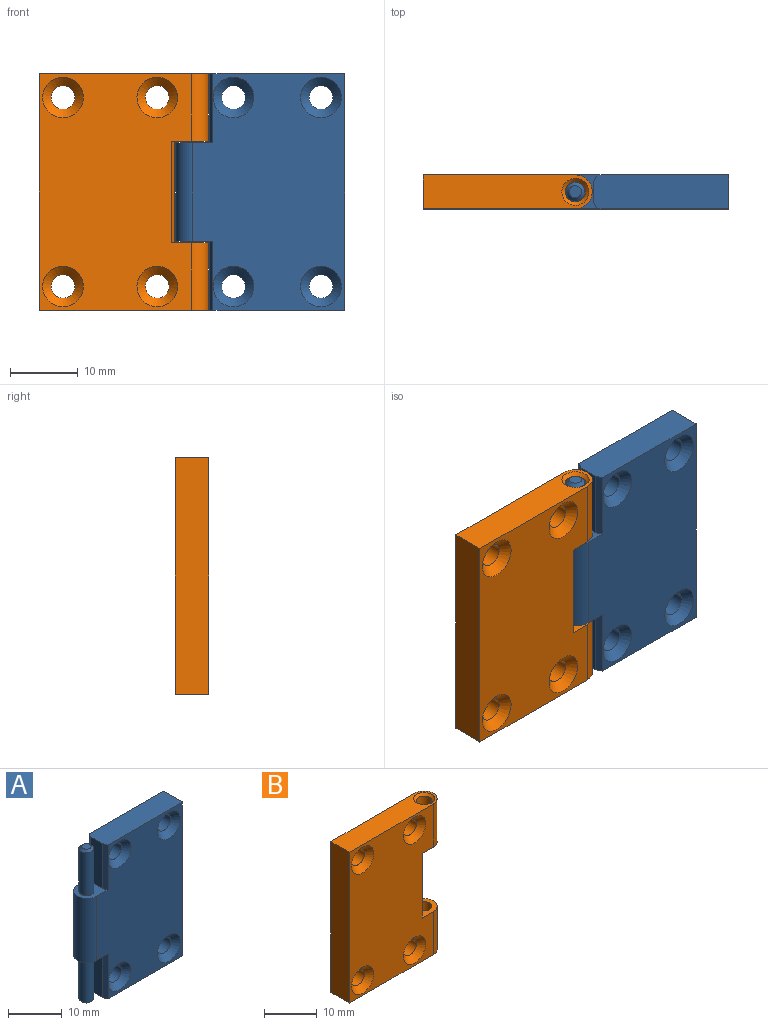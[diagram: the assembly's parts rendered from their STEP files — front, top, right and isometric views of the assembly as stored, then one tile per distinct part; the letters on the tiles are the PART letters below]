
ASSEMBLY  parts=2 mates=1
PART A: 28 faces, bbox 25x5x35 mm
  f0: plane 35x22.5mm, normal (0,-1,0), area 613.2mm2, adj f2,f3,f4,f5,f8,f12,f17,f19
  f1: plane 35x22.5mm, normal (0,1,0), area 687.8mm2, adj f2,f3,f4,f5,f8,f12,f16,f18
  f2: cylinder r=2.5mm len=14.6mm, axis (0,0,1), area 114.7mm2, adj f0,f1,f8,f12
  f3: plane 20x5mm, normal (0,0,-1), area 99.5mm2, adj f0,f1,f4,f10,f24,f26
  f4: plane 35x5mm, normal (1,0,0), area 175mm2, adj f0,f1,f3,f5
  f5: plane 20x5mm, normal (0,0,1), area 99.5mm2, adj f0,f1,f4,f6,f25,f27
  f6: plane 10.2x3mm, normal (-1,0,0), area 30.6mm2, adj f5,f8,f25,f27
  f7: cylinder r=1.4mm len=9.7mm, axis (0,0,1), area 85.3mm2, adj f8,f14
  f8: plane 5.5x5mm, normal (0,0,1), area 16.7mm2, adj f0,f1,f2,f6,f7,f25,f27
  f9: plane 1.8x1.8mm, normal (0,0,1), area 2.5mm2, adj f14
  f10: plane 10.2x3mm, normal (-1,0,0), area 30.6mm2, adj f3,f12,f24,f26
  f11: cylinder r=1.4mm len=9.7mm, axis (0,0,-1), area 85.3mm2, adj f12,f15
  f12: plane 5.5x5mm, normal (0,0,-1), area 16.7mm2, adj f0,f1,f2,f10,f11,f24,f26
  f13: plane 1.8x1.8mm, normal (0,0,-1), area 2.5mm2, adj f15
  f14: cone r=0.9mm half-angle=45deg, axis (0,0,-1), area 5.1mm2, adj f7,f9
  f15: cone r=0.9mm half-angle=45deg, axis (0,0,1), area 5.1mm2, adj f11,f13
  f16: cylinder r=1.75mm len=3.75mm, axis (0,-1,0), area 41.2mm2, adj f1,f17
  f17: cone r=1.75mm half-angle=45deg, axis (0,-1,0), area 26.4mm2, adj f0,f16
  f18: cylinder r=1.75mm len=3.75mm, axis (0,-1,0), area 41.2mm2, adj f1,f19
  f19: cone r=1.75mm half-angle=45deg, axis (0,-1,0), area 26.4mm2, adj f0,f18
  f20: cylinder r=1.75mm len=3.75mm, axis (0,-1,0), area 41.2mm2, adj f1,f21
  f21: cone r=1.75mm half-angle=45deg, axis (0,-1,0), area 26.4mm2, adj f0,f20
  f22: cylinder r=1.75mm len=3.75mm, axis (0,-1,0), area 41.2mm2, adj f1,f23
  f23: cone r=1.75mm half-angle=45deg, axis (0,-1,0), area 26.4mm2, adj f0,f22
  f24: plane 10.2x1mm, normal (-0.89,0.45,0), area 11.4mm2, adj f1,f3,f10,f12
  f25: plane 10.2x1mm, normal (-0.89,0.45,0), area 11.4mm2, adj f1,f5,f6,f8
  f26: plane 10.2x1mm, normal (-0.89,-0.45,0), area 11.4mm2, adj f0,f3,f10,f12
  f27: plane 10.2x1mm, normal (-0.89,-0.45,0), area 11.4mm2, adj f0,f5,f6,f8
PART B: 24 faces, bbox 25x5x35 mm
  f0: plane 15x3mm, normal (1,0,0), area 45mm2, adj f7,f9,f14,f15
  f1: plane 35x5mm, normal (-1,0,0), area 175mm2, adj f2,f3,f4,f5
  f2: plane 25x5mm, normal (0,0,-1), area 109.8mm2, adj f1,f4,f5,f8,f13
  f3: plane 25x5mm, normal (0,0,1), area 109.8mm2, adj f1,f4,f5,f6,f12
  f4: plane 35x22.5mm, normal (0,-1,0), area 629.4mm2, adj f1,f2,f3,f6,f7,f8,f9,f15
  f5: plane 35x22.5mm, normal (0,1,0), area 704mm2, adj f1,f2,f3,f6,f7,f8,f9,f14
  f6: cylinder r=2.5mm len=10mm, axis (0,0,1), area 78.5mm2, adj f3,f4,f5,f7
  f7: plane 5.5x5mm, normal (0,0,-1), area 15.7mm2, adj f0,f4,f5,f6,f11,f14,f15
  f8: cylinder r=2.5mm len=10mm, axis (0,0,-1), area 78.5mm2, adj f2,f4,f5,f9
  f9: plane 5.5x5mm, normal (0,0,1), area 15.7mm2, adj f0,f4,f5,f8,f10,f14,f15
  f10: cylinder r=1.5mm len=9.5mm, axis (0,0,-1), area 89.5mm2, adj f9,f13
  f11: cylinder r=1.5mm len=9.5mm, axis (0,0,-1), area 89.5mm2, adj f7,f12
  f12: cone r=2mm half-angle=45deg, axis (0,0,1), area 7.8mm2, adj f3,f11
  f13: cone r=1.5mm half-angle=45deg, axis (0,0,-1), area 7.8mm2, adj f2,f10
  f14: plane 15x1mm, normal (0.89,0.45,0), area 16.8mm2, adj f0,f5,f7,f9
  f15: plane 15x1mm, normal (0.89,-0.45,0), area 16.8mm2, adj f0,f4,f7,f9
  f16: cylinder r=1.75mm len=3.75mm, axis (0,-1,0), area 41.2mm2, adj f5,f17
  f17: cone r=1.75mm half-angle=45deg, axis (0,-1,0), area 26.4mm2, adj f4,f16
  f18: cylinder r=1.75mm len=3.75mm, axis (0,-1,0), area 41.2mm2, adj f5,f19
  f19: cone r=1.75mm half-angle=45deg, axis (0,-1,0), area 26.4mm2, adj f4,f18
  f20: cylinder r=1.75mm len=3.75mm, axis (0,-1,0), area 41.2mm2, adj f5,f21
  f21: cone r=1.75mm half-angle=45deg, axis (0,-1,0), area 26.4mm2, adj f4,f20
  f22: cylinder r=1.75mm len=3.75mm, axis (0,-1,0), area 41.2mm2, adj f5,f23
  f23: cone r=1.75mm half-angle=45deg, axis (0,-1,0), area 26.4mm2, adj f4,f22
PLACE A t=(0.18,6.2,-0.06)mm
PLACE B t=(-25.02,6.2,-0.06)mm
MATE revolute A.f7 <-> B.f8  axis (0,0,1) through (-12.52,6.2,17.44)mm
